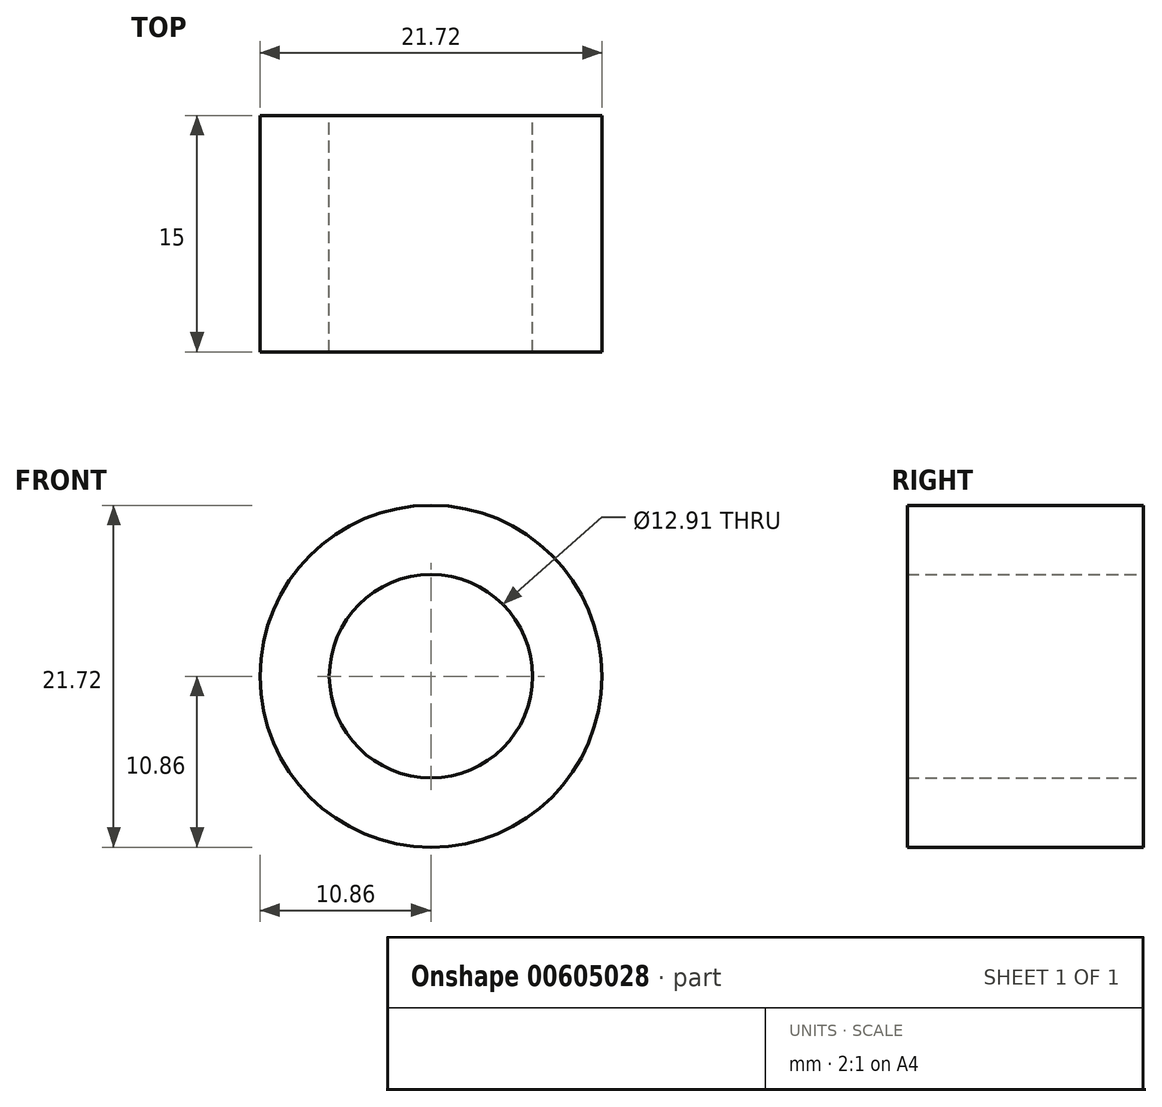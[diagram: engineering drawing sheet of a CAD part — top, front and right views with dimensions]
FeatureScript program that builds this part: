
annotation { "Feature Type Name" : "Feature", "Feature Type Description" : "" }
export const myFeature = defineFeature(function(context is Context, id is Id, definition is map)
    precondition{}
    {
        {
            var Q0;
            Q0=qCreatedBy(makeId("Front.planeOp"),FACE);
            var sketch = newSketch(context, id + "F0", { "sketchPlane" : qUnion([Q0])});
            skCircle(sketch, "E0", {"center": v(0, 0) * mm, "radius": 10.86 * mm});
            skCircle(sketch, "E1", {"center": v(0, 0) * mm, "radius": 6.45 * mm});
            skSolve(sketch);
        }
        {
            var Q0;
            Q0=makeQuery(id+"F0.imprint","IMPRINT",FACE,{"disambiguationData":[TD([[makeQuery(id+"F0.imprint","IMPRINT",EDGE,{"derivedFrom":sQuery(id+"F0.wireOp",EDGE,"E0")}),1.0]])]});
            extrude(context, id + "F1", {"entities" : qUnion([Q0]), "depth" : 15 * mm, "offsetDistance" : 25 * mm});
        }
    });
